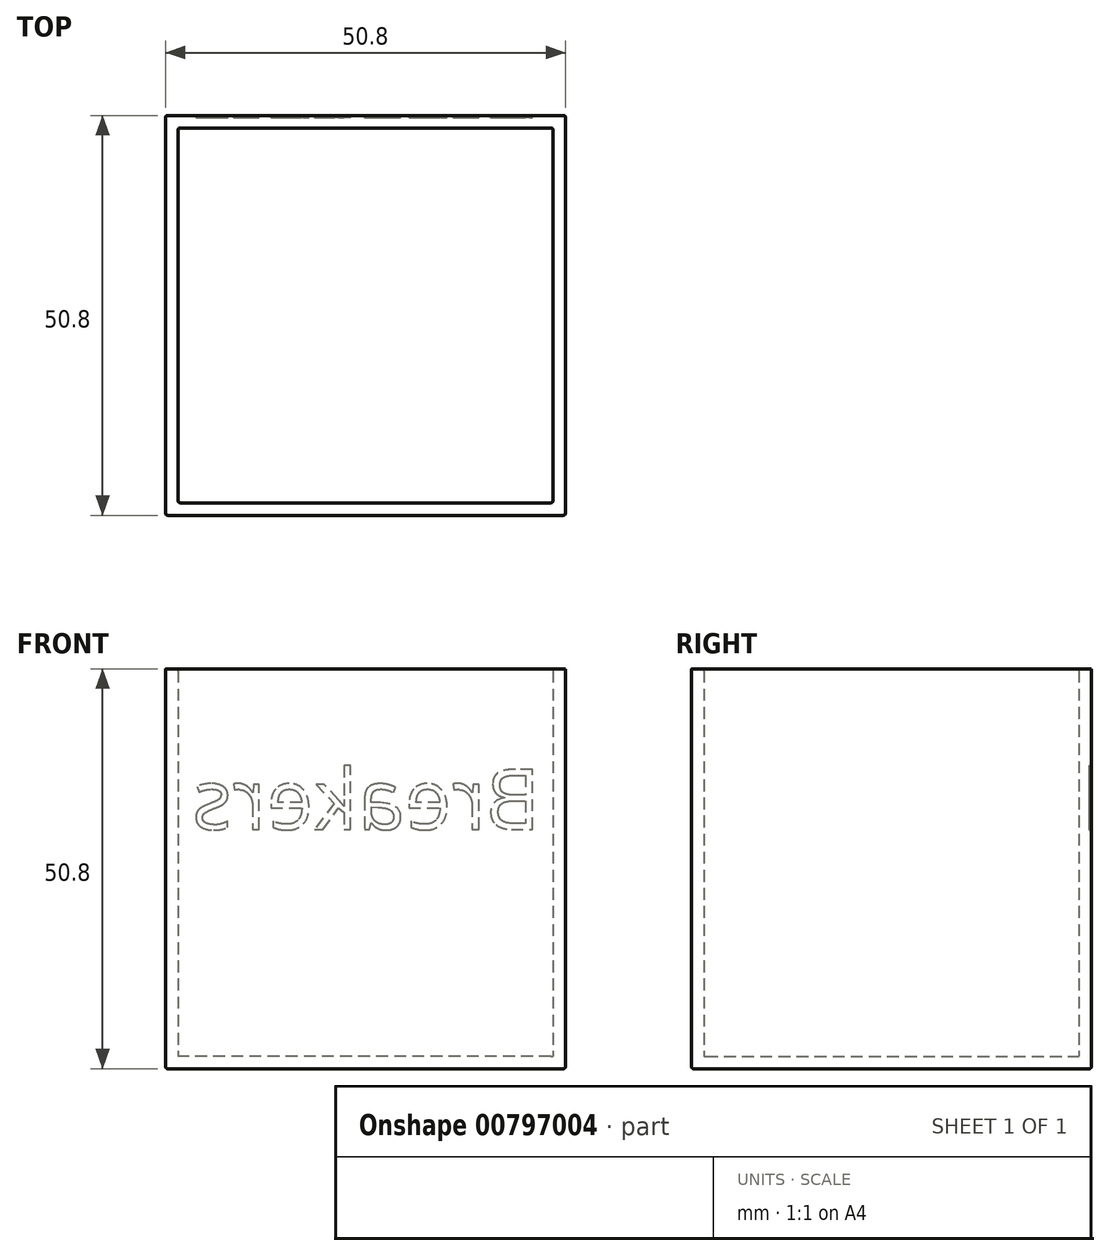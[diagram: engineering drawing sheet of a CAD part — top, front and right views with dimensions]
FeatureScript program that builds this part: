
annotation { "Feature Type Name" : "Feature", "Feature Type Description" : "" }
export const myFeature = defineFeature(function(context is Context, id is Id, definition is map)
    precondition{}
    {
        {
            var Q0;
            Q0=qCreatedBy(makeId("Top.planeOp"),FACE);
            var sketch = newSketch(context, id + "F0", { "sketchPlane" : qUnion([Q0])});
            skLineSegment(sketch, "E0.bottom", {"start": v(25.4, -25.4) * mm, "end": v(-25.4, -25.4) * mm});
            skLineSegment(sketch, "E0.top", {"start": v(25.4, 25.4) * mm, "end": v(-25.4, 25.4) * mm});
            skLineSegment(sketch, "E0.left", {"start": v(25.4, -25.4) * mm, "end": v(25.4, 25.4) * mm});
            skLineSegment(sketch, "E0.right", {"start": v(-25.4, -25.4) * mm, "end": v(-25.4, 25.4) * mm});
            skPoint(sketch, "E0.middle", {"position": v(0, 0) * mm});
            skSolve(sketch);
        }
        {
            var Q0;
            Q0 = qSketchRegion(id + "F0", true);
            extrude(context, id + "F1", {"entities" : qUnion([Q0]), "depth" : 1.59 * mm, "offsetDistance" : 25.4 * mm});
        }
        {
            var Q0;
            Q0=makeQuery(id+"F1.opExtrude","CAP_FACE",FACE,{"disambiguationData":[OSD([sQuery(id+"F0.wireOp",EDGE,"E0.bottom"),sQuery(id+"F0.wireOp",EDGE,"E0.top"),sQuery(id+"F0.wireOp",EDGE,"E0.left"),sQuery(id+"F0.wireOp",EDGE,"E0.right")])],"isStart":false});
            var sketch = newSketch(context, id + "F2", { "sketchPlane" : qUnion([Q0])});
            skLineSegment(sketch, "E1.bottom", {"start": v(25.4, -25.4) * mm, "end": v(-25.4, -25.4) * mm});
            skLineSegment(sketch, "E1.top", {"start": v(25.4, 25.4) * mm, "end": v(-25.4, 25.4) * mm});
            skLineSegment(sketch, "E1.left", {"start": v(25.4, -25.4) * mm, "end": v(25.4, 25.4) * mm});
            skLineSegment(sketch, "E1.right", {"start": v(-25.4, -25.4) * mm, "end": v(-25.4, 25.4) * mm});
            skPoint(sketch, "E1.middle", {"position": v(0, 0) * mm});
            skLineSegment(sketch, "E2.0", {"start": v(23.81, 23.81) * mm, "end": v(-23.81, 23.81) * mm});
            skLineSegment(sketch, "E2.1", {"start": v(23.81, -23.81) * mm, "end": v(23.81, 23.81) * mm});
            skLineSegment(sketch, "E2.2", {"start": v(23.81, -23.81) * mm, "end": v(-23.81, -23.81) * mm});
            skLineSegment(sketch, "E2.3", {"start": v(-23.81, -23.81) * mm, "end": v(-23.81, 23.81) * mm});
            skSolve(sketch);
        }
        {
            var Q0;
            Q0 = qSketchRegion(id + "F2", true);
            extrude(context, id + "F3", {"entities" : qUnion([Q0]), "operationType" : NewBodyOperationType.ADD, "depth" : 49.2 * mm, "offsetDistance" : 25.4 * mm});
        }
        {
            var Q0;
            Q0=makeQuery(id+"F3.opExtrude","CAP_EDGE",EDGE,{"disambiguationData":[OSD([sQuery(id+"F2.wireOp",EDGE,"E2.3")])],"isStart":true});
            var Q1;
            Q1=makeQuery(id+"F3.opExtrude","SWEPT_EDGE",EDGE,{"disambiguationData":[OSD([sQuery(id+"F2.wireOp",EDGE,"E2.2"),sQuery(id+"F2.wireOp",EDGE,"E2.3")])]});
            var Q2;
            Q2=makeQuery(id+"F3.opExtrude","CAP_EDGE",EDGE,{"disambiguationData":[OSD([sQuery(id+"F2.wireOp",EDGE,"E2.2")])],"isStart":true});
            var Q3;
            Q3=makeQuery(id+"F3.opExtrude","CAP_EDGE",EDGE,{"disambiguationData":[OSD([sQuery(id+"F2.wireOp",EDGE,"E2.3")])],"isStart":false});
            var Q4;
            Q4=makeQuery(id+"F3.opExtrude","CAP_EDGE",EDGE,{"disambiguationData":[OSD([sQuery(id+"F2.wireOp",EDGE,"E2.2")])],"isStart":false});
            var Q5;
            Q5=makeQuery(id+"F3.opExtrude","CAP_EDGE",EDGE,{"disambiguationData":[OSD([sQuery(id+"F2.wireOp",EDGE,"E2.0")])],"isStart":true});
            var Q6;
            Q6=makeQuery(id+"F3.opExtrude","SWEPT_EDGE",EDGE,{"disambiguationData":[OSD([sQuery(id+"F2.wireOp",EDGE,"E2.0"),sQuery(id+"F2.wireOp",EDGE,"E2.3")])]});
            var Q7;
            Q7=makeQuery(id+"F3.opExtrude","CAP_EDGE",EDGE,{"disambiguationData":[OSD([sQuery(id+"F2.wireOp",EDGE,"E2.0")])],"isStart":false});
            var Q8;
            Q8=makeQuery(id+"F3.opExtrude","SWEPT_EDGE",EDGE,{"disambiguationData":[OSD([sQuery(id+"F2.wireOp",EDGE,"E2.0"),sQuery(id+"F2.wireOp",EDGE,"E2.1")])]});
            var Q9;
            Q9=makeQuery(id+"F3.opExtrude","CAP_EDGE",EDGE,{"disambiguationData":[OSD([sQuery(id+"F2.wireOp",EDGE,"E2.1")])],"isStart":true});
            var Q10;
            Q10=makeQuery(id+"F3.opExtrude","CAP_EDGE",EDGE,{"disambiguationData":[OSD([sQuery(id+"F2.wireOp",EDGE,"E2.1")])],"isStart":false});
            var Q11;
            Q11=makeQuery(id+"F3.opExtrude","SWEPT_EDGE",EDGE,{"disambiguationData":[OSD([sQuery(id+"F2.wireOp",EDGE,"E2.1"),sQuery(id+"F2.wireOp",EDGE,"E2.2")])]});
            var Q12;
            Q12=makeQuery(id+"F3.boolean.opBoolean","MERGE",EDGE,{"derivedFrom":[makeQuery(id+"F1.opExtrude","SWEPT_EDGE",EDGE,{"disambiguationData":[OSD([sQuery(id+"F0.wireOp",EDGE,"E0.bottom"),sQuery(id+"F0.wireOp",EDGE,"E0.right")])]}),makeQuery(id+"F3.opExtrude","SWEPT_EDGE",EDGE,{"disambiguationData":[OSD([sQuery(id+"F2.wireOp",EDGE,"E1.bottom"),sQuery(id+"F2.wireOp",EDGE,"E1.right")])]})]});
            var Q13;
            Q13=makeQuery(id+"F3.boolean.opBoolean","MERGE",EDGE,{"derivedFrom":[makeQuery(id+"F1.opExtrude","SWEPT_EDGE",EDGE,{"disambiguationData":[OSD([sQuery(id+"F0.wireOp",EDGE,"E0.bottom"),sQuery(id+"F0.wireOp",EDGE,"E0.left")])]}),makeQuery(id+"F3.opExtrude","SWEPT_EDGE",EDGE,{"disambiguationData":[OSD([sQuery(id+"F2.wireOp",EDGE,"E1.bottom"),sQuery(id+"F2.wireOp",EDGE,"E1.left")])]})]});
            var Q14;
            Q14=makeQuery(id+"F3.boolean.opBoolean","MERGE",EDGE,{"derivedFrom":[makeQuery(id+"F1.opExtrude","SWEPT_EDGE",EDGE,{"disambiguationData":[OSD([sQuery(id+"F0.wireOp",EDGE,"E0.top"),sQuery(id+"F0.wireOp",EDGE,"E0.left")])]}),makeQuery(id+"F3.opExtrude","SWEPT_EDGE",EDGE,{"disambiguationData":[OSD([sQuery(id+"F2.wireOp",EDGE,"E1.top"),sQuery(id+"F2.wireOp",EDGE,"E1.left")])]})]});
            var Q15;
            Q15=makeQuery(id+"F3.boolean.opBoolean","MERGE",EDGE,{"derivedFrom":[makeQuery(id+"F1.opExtrude","SWEPT_EDGE",EDGE,{"disambiguationData":[OSD([sQuery(id+"F0.wireOp",EDGE,"E0.top"),sQuery(id+"F0.wireOp",EDGE,"E0.right")])]}),makeQuery(id+"F3.opExtrude","SWEPT_EDGE",EDGE,{"disambiguationData":[OSD([sQuery(id+"F2.wireOp",EDGE,"E1.top"),sQuery(id+"F2.wireOp",EDGE,"E1.right")])]})]});
            var Q16;
            Q16=makeQuery(id+"F1.opExtrude","CAP_EDGE",EDGE,{"disambiguationData":[OSD([sQuery(id+"F0.wireOp",EDGE,"E0.right")])],"isStart":true});
            var Q17;
            Q17=makeQuery(id+"F1.opExtrude","CAP_EDGE",EDGE,{"disambiguationData":[OSD([sQuery(id+"F0.wireOp",EDGE,"E0.bottom")])],"isStart":true});
            var Q18;
            Q18=makeQuery(id+"F1.opExtrude","CAP_EDGE",EDGE,{"disambiguationData":[OSD([sQuery(id+"F0.wireOp",EDGE,"E0.top")])],"isStart":true});
            var Q19;
            Q19=makeQuery(id+"F1.opExtrude","CAP_EDGE",EDGE,{"disambiguationData":[OSD([sQuery(id+"F0.wireOp",EDGE,"E0.left")])],"isStart":true});
            fillet(context, id + "F4", {"entities" : qUnion([Q0, Q1, Q2, Q3, Q4, Q5, Q6, Q7, Q8, Q9, Q10, Q11, Q12, Q13, Q14, Q15, Q16, Q17, Q18, Q19]), "radius" : 0.25 * mm, "tangentPropagation" : true, "allowEdgeOverflow" : false});
        }
        {
            var Q0;
            Q0=makeQuery(id+"F3.boolean.opBoolean","MERGE",FACE,{"derivedFrom":[makeQuery(id+"F1.opExtrude","SWEPT_FACE",FACE,{"disambiguationData":[OSD([sQuery(id+"F0.wireOp",EDGE,"E0.top")])]}),makeQuery(id+"F3.opExtrude","SWEPT_FACE",FACE,{"disambiguationData":[OSD([sQuery(id+"F2.wireOp",EDGE,"E1.top")])]})]});
            var sketch = newSketch(context, id + "F5", { "sketchPlane" : qUnion([Q0])});
            skText(sketch, "E3", { "text": "Breakers", "fontName": "OpenSans-Regular.ttf"});
            const initialGuessF5  = {"E3": [-0.02223, 0.03041, 1, 0, 0.00769]};
            skSetInitialGuess(sketch, initialGuessF5);
            skSolve(sketch);
        }
        {
            var Q0;
            Q0 = qSketchRegion(id + "F5", true);
            extrude(context, id + "F6", {"entities" : qUnion([Q0]), "operationType" : NewBodyOperationType.REMOVE, "oppositeDirection" : true, "depth" : 0.25 * mm, "offsetDistance" : 25.4 * mm});
        }
    });
